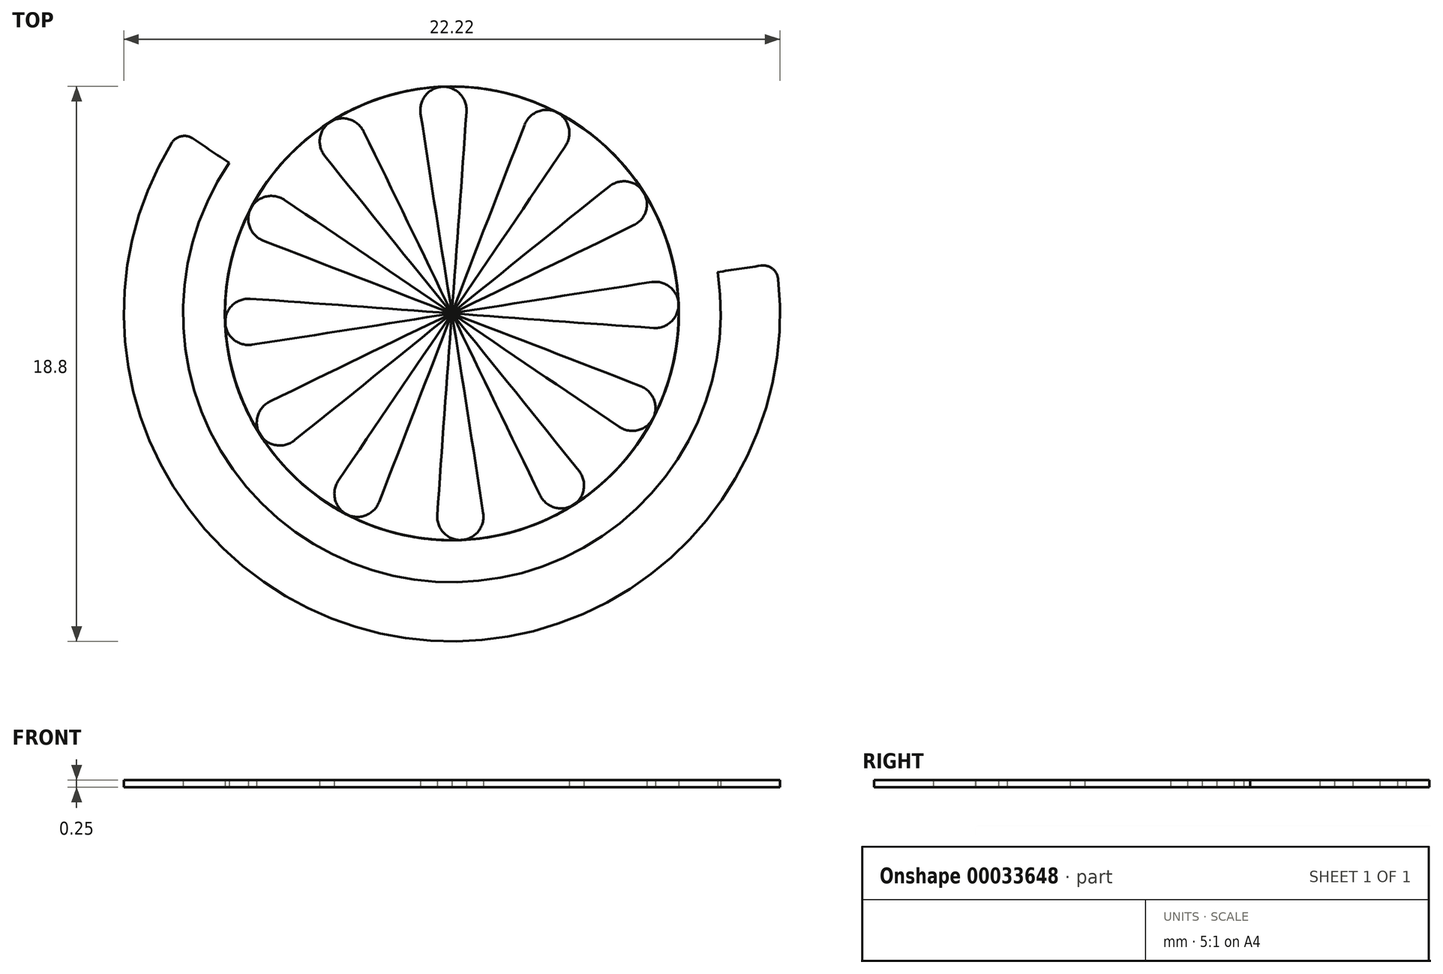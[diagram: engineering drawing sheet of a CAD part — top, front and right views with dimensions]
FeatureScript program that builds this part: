
annotation { "Feature Type Name" : "Feature", "Feature Type Description" : "" }
export const myFeature = defineFeature(function(context is Context, id is Id, definition is map)
    precondition{}
    {
        {
            assignVariable(context, id + "F0", {"name" : "N", "anyValue" : 12});
        }
        {
            assignVariable(context, id + "F1", {"name" : "Swid", "anyValue" : 0.25});
        }
        {
            var Q0;
            Q0=qCreatedBy(makeId("Top.planeOp"),FACE);
            var sketch = newSketch(context, id + "F2", { "sketchPlane" : qUnion([Q0])});
            skCircle(sketch, "E0", {"center": v(0, 0) * mm, "radius": 9.1 * mm, "construction": true});
            skCircle(sketch, "E1", {"center": v(0, 0) * mm, "radius": 9.53 * mm, "construction": true});
            skCircle(sketch, "E2", {"center": v(0, 0) * mm, "radius": 11.11 * mm});
            skLineSegment(sketch, "E3", {"start": v(0, 0) * mm, "end": v(0, 9.1) * mm, "construction": true});
            skLineSegment(sketch, "E4", {"start": v(0, 0) * mm, "end": v(0.6, 9.09) * mm, "construction": true});
            skLineSegment(sketch, "E5", {"start": v(0, 0) * mm, "end": v(1.19, 9.03) * mm, "construction": true});
            skLineSegment(sketch, "E6", {"start": v(0, 0) * mm, "end": v(1.78, 8.93) * mm, "construction": true});
            skLineSegment(sketch, "E7", {"start": v(0, 0) * mm, "end": v(2.36, 8.8) * mm, "construction": true});
            skCircle(sketch, "E8", {"center": v(0, 0) * mm, "radius": 7.69 * mm});
            skLineSegment(sketch, "E9", {"start": v(0.6, 9.09) * mm, "end": v(0, 9.13) * mm, "construction": true});
            skLineSegment(sketch, "E10", {"start": v(1.19, 9.03) * mm, "end": v(0, 9.19) * mm, "construction": true});
            skLineSegment(sketch, "E11", {"start": v(1.78, 8.93) * mm, "end": v(0.02, 9.28) * mm, "construction": true});
            skLineSegment(sketch, "E12", {"start": v(2.36, 8.8) * mm, "end": v(0.05, 9.42) * mm, "construction": true});
            skLineSegment(sketch, "E13", {"start": v(0, 0) * mm, "end": v(2.93, 8.63) * mm, "construction": true});
            skLineSegment(sketch, "E14", {"start": v(2.93, 8.63) * mm, "end": v(0.1, 9.58) * mm, "construction": true});
            skLineSegment(sketch, "E15", {"start": v(0, 0) * mm, "end": v(3.49, 8.42) * mm, "construction": true});
            skLineSegment(sketch, "E16", {"start": v(0, 0) * mm, "end": v(4.03, 8.17) * mm, "construction": true});
            skLineSegment(sketch, "E17", {"start": v(0, 0) * mm, "end": v(4.55, 7.89) * mm, "construction": true});
            skLineSegment(sketch, "E18", {"start": v(3.49, 8.42) * mm, "end": v(0.18, 9.78) * mm, "construction": true});
            skLineSegment(sketch, "E19", {"start": v(4.03, 8.17) * mm, "end": v(0.29, 10.02) * mm, "construction": true});
            skLineSegment(sketch, "E20", {"start": v(4.55, 7.89) * mm, "end": v(0.42, 10.27) * mm, "construction": true});
            skLineSegment(sketch, "E21", {"start": v(0, 0) * mm, "end": v(5.06, 7.57) * mm, "construction": true});
            skLineSegment(sketch, "E22", {"start": v(0, 0) * mm, "end": v(5.55, 7.23) * mm, "construction": true});
            skLineSegment(sketch, "E23", {"start": v(0, 0) * mm, "end": v(6, 6.85) * mm, "construction": true});
            skLineSegment(sketch, "E24", {"start": v(0, 0) * mm, "end": v(6.44, 6.44) * mm, "construction": true});
            skLineSegment(sketch, "E25", {"start": v(0, 0) * mm, "end": v(6.85, 6) * mm, "construction": true});
            skLineSegment(sketch, "E26", {"start": v(5.06, 7.57) * mm, "end": v(0.6, 10.55) * mm, "construction": true});
            skLineSegment(sketch, "E27", {"start": v(5.55, 7.23) * mm, "end": v(0.82, 10.86) * mm, "construction": true});
            skLineSegment(sketch, "E28", {"start": v(6, 6.85) * mm, "end": v(1.08, 11.17) * mm, "construction": true});
            skLineSegment(sketch, "E29", {"start": v(6.44, 6.44) * mm, "end": v(1.38, 11.5) * mm, "construction": true});
            skLineSegment(sketch, "E30", {"start": v(6.85, 6) * mm, "end": v(1.74, 11.83) * mm, "construction": true});
            skLineSegment(sketch, "E31", {"start": v(0, 0) * mm, "end": v(7.23, 5.55) * mm, "construction": true});
            skLineSegment(sketch, "E32", {"start": v(7.23, 5.55) * mm, "end": v(2.15, 12.17) * mm, "construction": true});
            skLineSegment(sketch, "E33", {"start": v(0, 0) * mm, "end": v(7.57, 5.06) * mm, "construction": true});
            skLineSegment(sketch, "E34", {"start": v(7.57, 5.06) * mm, "end": v(2.6, 12.5) * mm, "construction": true});
            skSolve(sketch);
        }
        {
            var Q0;
            Q0=qCreatedBy(makeId("Top.planeOp"),FACE);
            var sketch = newSketch(context, id + "F3", { "sketchPlane" : qUnion([Q0])});
            skLineSegment(sketch, "E35.0", {"start": v(7.23, 5.55) * mm, "end": v(2.15, 12.17) * mm, "construction": true});
            skLineSegment(sketch, "E35.1", {"start": v(6.85, 6) * mm, "end": v(1.74, 11.83) * mm, "construction": true});
            skLineSegment(sketch, "E35.2", {"start": v(6.44, 6.44) * mm, "end": v(1.38, 11.5) * mm, "construction": true});
            skLineSegment(sketch, "E35.3", {"start": v(6, 6.85) * mm, "end": v(1.08, 11.17) * mm, "construction": true});
            skLineSegment(sketch, "E35.4", {"start": v(5.55, 7.23) * mm, "end": v(0.82, 10.86) * mm, "construction": true});
            skLineSegment(sketch, "E35.5", {"start": v(5.06, 7.57) * mm, "end": v(0.6, 10.55) * mm, "construction": true});
            skLineSegment(sketch, "E35.6", {"start": v(4.55, 7.89) * mm, "end": v(0.42, 10.27) * mm, "construction": true});
            skLineSegment(sketch, "E35.7", {"start": v(4.03, 8.17) * mm, "end": v(0.29, 10.02) * mm, "construction": true});
            skLineSegment(sketch, "E35.8", {"start": v(3.49, 8.42) * mm, "end": v(0.18, 9.78) * mm, "construction": true});
            skLineSegment(sketch, "E35.9", {"start": v(2.93, 8.63) * mm, "end": v(0.1, 9.58) * mm, "construction": true});
            skLineSegment(sketch, "E35.10", {"start": v(2.36, 8.8) * mm, "end": v(0.05, 9.42) * mm, "construction": true});
            skLineSegment(sketch, "E35.11", {"start": v(1.78, 8.93) * mm, "end": v(0.02, 9.28) * mm, "construction": true});
            skLineSegment(sketch, "E35.12", {"start": v(1.19, 9.03) * mm, "end": v(0, 9.19) * mm, "construction": true});
            skLineSegment(sketch, "E35.13", {"start": v(0.6, 9.09) * mm, "end": v(0, 9.13) * mm, "construction": true});
            skCircle(sketch, "E35.14", {"center": v(0, 0) * mm, "radius": 9.1 * mm});
            skCircle(sketch, "E35.15", {"center": v(0, 0) * mm, "radius": 7.69 * mm});
            skCircle(sketch, "E35.16", {"center": v(0, 0) * mm, "radius": 9.53 * mm, "construction": true});
            skCircle(sketch, "E35.17", {"center": v(0, 0) * mm, "radius": 11.11 * mm});
            skLineSegment(sketch, "E36.0", {"start": v(7.57, 5.06) * mm, "end": v(2.6, 12.5) * mm, "construction": true});
            skLineSegment(sketch, "E37.0", {"start": v(0, 0) * mm, "end": v(0, 9.1) * mm, "construction": true});
            skFitSpline(sketch, "E38", {"points": [v(0, 20.8) * mm, v(0.04, 21.12) * mm, v(0.3, 22.04) * mm, v(0.97, 23.47) * mm, v(2.25, 25.28) * mm, v(4.27, 27.28) * mm, v(7.12, 29.27) * mm, v(10.86, 31) * mm, v(15.45, 32.22) * mm, v(20.8, 32.68) * mm, v(26.8, 32.15) * mm, v(33.21, 30.42) * mm, v(39.8, 27.34) * mm, v(46.28, 22.79) * mm, v(52.32, 16.74) * mm, v(57.58, 9.22) * mm, v(0, 0) * mm], "startDerivative": vector(7.54, 64.54) * mm, "endDerivative": vector(-870.75, -139.39) * mm});
            skLineSegment(sketch, "E39", {"start": v(2.27, 25.3) * mm, "end": v(0, 0) * mm, "construction": true});
            skLineSegment(sketch, "E40", {"start": v(0, 0) * mm, "end": v(6.47, 28.92) * mm, "construction": true});
            skFitSpline(sketch, "E41.MirrorCS", {"points": [v(8.87, 18.82) * mm, v(8.97, 19.12) * mm, v(9.13, 20.06) * mm, v(9.13, 21.64) * mm, v(8.74, 23.82) * mm, v(7.77, 26.5) * mm, v(6.04, 29.52) * mm, v(3.4, 32.67) * mm, v(-0.23, 35.73) * mm, v(-4.89, 38.43) * mm, v(-10.53, 40.5) * mm, v(-17.07, 41.68) * mm, v(-24.35, 41.7) * mm, v(-32.15, 40.35) * mm, v(-40.19, 37.45) * mm, v(-48.15, 32.89) * mm, v(0, 0) * mm], "startDerivative": vector(20.7, 61.6) * mm, "endDerivative": vector(728.2, -497.34) * mm});
            skLineSegment(sketch, "E42", {"start": v(8.87, 18.82) * mm, "end": v(8.74, 18.55) * mm});
            skLineSegment(sketch, "E43", {"start": v(0, 20.81) * mm, "end": v(0, 20.5) * mm});
            skSolve(sketch);
        }
        {
            var Q0;
            {var subQ3=sQuery(id+"F3.wireOp",EDGE,"E41.MirrorCS");var subQ6=sQuery(id+"F3.wireOp",EDGE,"E35.17");var subQ8=makeQuery(id+"F3.imprint","INTERSECT",VERTEX,{"disambiguationData":[OD(1.0)],"derivedFrom":[subQ6,subQ3]});Q0=makeQuery(id+"F3.imprint","IMPRINT",FACE,{"disambiguationData":[TD([[makeQuery(id+"F3.imprint","IMPRINT",EDGE,{"disambiguationData":[TD([[subQ8,-1.0]])],"derivedFrom":subQ6}),1.0]])]});}
            var Q1;
            {var subQ3=sQuery(id+"F3.wireOp",EDGE,"E41.MirrorCS");var subQ5=sQuery(id+"F3.wireOp",EDGE,"E35.15");var subQ6=makeQuery(id+"F3.imprint","INTERSECT",VERTEX,{"derivedFrom":[subQ5,subQ3]});Q1=makeQuery(id+"F3.imprint","IMPRINT",FACE,{"disambiguationData":[TD([[makeQuery(id+"F3.imprint","IMPRINT",EDGE,{"disambiguationData":[TD([[subQ6,-1.0]])],"derivedFrom":subQ5}),1.0]])]});}
            var Q2;
            {var subQ2=sQuery(id+"F3.wireOp",EDGE,"E42");Q2=makeQuery(id+"F3.imprint","IMPRINT",FACE,{"disambiguationData":[TD([[makeQuery(id+"F3.imprint","IMPRINT",EDGE,{"derivedFrom":subQ2}),-1.0]])]});}
            var Q3;
            {var subQ1=sQuery(id+"F3.wireOp",EDGE,"E35.14");var subQ3=sQuery(id+"F3.wireOp",EDGE,"E38");var subQ4=makeQuery(id+"F3.imprint","INTERSECT",VERTEX,{"derivedFrom":[subQ1,subQ3]});Q3=makeQuery(id+"F3.imprint","IMPRINT",FACE,{"disambiguationData":[TD([[makeQuery(id+"F3.imprint","IMPRINT",EDGE,{"disambiguationData":[TD([[subQ4,1.0]])],"derivedFrom":subQ3}),1.0]])]});}
            var Q4;
            {var subQ0=sQuery(id+"F3.wireOp",EDGE,"E43");Q4=makeQuery(id+"F3.imprint","IMPRINT",FACE,{"disambiguationData":[TD([[makeQuery(id+"F3.imprint","IMPRINT",EDGE,{"derivedFrom":subQ0}),1.0]])]});}
            extrude(context, id + "F4", {"entities" : qUnion([Q0, Q1, Q2, Q3, Q4]), "depth" : (getVariable(context, 'Swid')) * mm, "offsetDistance" : 25.4 * mm});
        }
        {
            var Q0;
            Q0=qCreatedBy(makeId("Right.planeOp"),FACE);
            var sketch = newSketch(context, id + "F5", { "sketchPlane" : qUnion([Q0])});
            skLineSegment(sketch, "E44", {"start": v(0, 0) * mm, "end": v(0, 43.3) * mm, "construction": true});
            skSolve(sketch);
        }
        {
            var Q0;
            Q0=makeQuery(id+"F4.opExtrude","SWEPT_EDGE",EDGE,{"disambiguationData":[OSD([sQuery(id+"F3.wireOp",EDGE,"E35.17"),sQuery(id+"F3.wireOp",EDGE,"E41.MirrorCS")])]});
            var Q1;
            Q1=makeQuery(id+"F4.opExtrude","SWEPT_EDGE",EDGE,{"disambiguationData":[OSD([sQuery(id+"F3.wireOp",EDGE,"E35.17"),sQuery(id+"F3.wireOp",EDGE,"E38")])]});
            fillet(context, id + "F6", {"entities" : qUnion([Q0, Q1]), "radius" : 0.5 * mm, "tangentPropagation" : true, "allowEdgeOverflow" : false});
        }
        {
            var Q0;
            Q0=makeQuery(id+"F4.opExtrude","SWEPT_EDGE",EDGE,{"disambiguationData":[OSD([sQuery(id+"F3.wireOp",EDGE,"E35.15"),sQuery(id+"F3.wireOp",EDGE,"E42")])]});
            var Q1;
            Q1=makeQuery(id+"F4.opExtrude","SWEPT_EDGE",EDGE,{"disambiguationData":[OSD([sQuery(id+"F3.wireOp",EDGE,"E35.15"),sQuery(id+"F3.wireOp",EDGE,"E43")])]});
            fillet(context, id + "F7", {"entities" : qUnion([Q0, Q1]), "radius" : 0.8 * mm, "tangentPropagation" : true, "allowEdgeOverflow" : false});
        }
        {
            var Q0;
            Q0=makeQuery(id+"F4.opExtrude","SWEPT_BODY",BODY,{"disambiguationData":[OSD([sQuery(id+"F3.wireOp",EDGE,"E35.15"),sQuery(id+"F3.wireOp",EDGE,"E35.17"),sQuery(id+"F3.wireOp",EDGE,"E38"),sQuery(id+"F3.wireOp",EDGE,"E41.MirrorCS"),sQuery(id+"F3.wireOp",EDGE,"9305e2c8-a00a-4cbc-a3b2-8fc88bc1717c"),sQuery(id+"F3.wireOp",EDGE,"f762f43d-eaf9-45ff-b6cd-062fd530227c")])]});
            var Q1;
            Q1=sQuery(id+"F5.wireOp",EDGE,"E44");
            circularPattern(context, id + "F8", {"operationType" : NewBodyOperationType.ADD, "entities" : qUnion([Q0]), "axis" : qUnion([Q1]), "angle" : (360 / getVariable(context, 'N')) * degree, "instanceCount" : getVariable(context, 'N'), "oppositeDirection" : true});
        }
    });
